# Revit family: IS_Contour21_S3111_BIM_DE
name_source: partatom
category: Plumbing Fixtures
revit_build: Autodesk Revit MEP 2016 (Build: 20161004_0715(x64)
units: mm (PartAtom-declared; Revit-internal decimal feet)

## family parameters
Cut with Voids When Loaded = No
Host = Face
OmniClass Number = 23.45.05.21.11.11
OmniClass Title = Water Operated Water Closets
Part Type = Normal
Room Calculation Point = No
Round Connector Dimension = Use Diameter
Shared = No

## types (2) — shared parameters
Accessories = www.idealstandard.de\ersatzteile
AreaUnits = millimeters
Assembly Code = C1030200
AssetType = Fixed
Brand = Ideal Standard
CodePerformance = DIN EN 997 CL1-6A, DIN EN 33, DIN
ConnectionType = Plumbing
CurrencyUnit = €
Default Elevation = 440 mm  [stored 1.44357 ft]
Description = CONTOUR 21 ZAVESNE WC S PLOCHYM SPLACH
DurationUnit = year
ExpectedLife = 25
Features = CONTOUR21 accessible wall mounted bowl 355x700mm, washout
Finish = White
GrossWeight = 23,9 kg
InstallationDate = 1900-12-31T23:59:59
InstallationInstructions = www.idealstandard.de\produkte
LinearUnits = millimeters
ManufacturerURL = www.idealstandard.de
Material = Vitreous china
NominalHeight = 376 mm
NominalLength = 700 mm
NominalWidth = 350 mm
ProductInformation = www.idealstandard.de
Shape = Sculptured
Size = 700 x 350 x 376 mm
Space = Internal
URL = www.idealstandard.de
Uniclass2015Code = Pr_40_20_93_94
Uniclass2015Title = WC pans
Uniclass2015Version = Products v1.1
Version = 1
VolumeUnits = Litres
zero-valued in all types: Cost, NominalDepth

## per-type parameters (varying)
| type | BIMObjectName | BarCode | Color | Model | ModelNumber | ModelReference | Name |
| S311101 - CONTOUR21 accessible wall mounted bowl 355x700mm, washout | ISI_IdealStandard_WCPans_CONTOUR 21_S311101 | 5017830482147 | White | S311101 | S311101 | IS Wandflachspül-WC CONTOUR 21, barrierefrei, 350x700x380mm, Weiß | ISI_IdealStandard_WCPans_CONTOUR 21_S311101 |
| S3111MA - CONTOUR21 accessible wall mounted bowl 355x700mm, washout | ISI_IdealStandard_WCPans_CONTOUR 21_S3111MA | 5017830482154 | White IP | S3111MA | S3111MA | IS Wandflachspül-WC CONTOUR 21, barrierefrei, 350x700x380mm, Weiß m. IP | ISI_IdealStandard_WCPans_CONTOUR 21_S3111MA |

note: [stored X ft] marks values corroborated as IEEE doubles in the binary element streams (Revit-internal decimal feet)

## geometry (parser evidence)
native form markers: Blend x4, Sweep x1
no freeform markers — native parametric forms only
